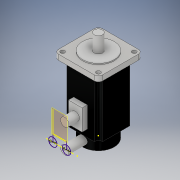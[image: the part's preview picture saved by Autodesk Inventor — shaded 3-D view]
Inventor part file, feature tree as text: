
AUTODESK INVENTOR PART (.ipt)
format: ipt  version: 2019.4 (Build 234330000, 330)  size: 254,464 bytes
history: native  units: mm
features: sketch x12, extrude x9, fillet x1, plane x1
ambient origin geometry x8: Origin, YZ Plane, XZ Plane, XY Plane, X Axis, Y Axis, Z Axis, Center Point
bodies: Solid1 (feature_tree)
feature tree (23):
  extrude  "Extrusion1"  Depth=34.0mm
  sketch  "Sketch4"  dims[d2=54.0mm d3=0.0mm d15=4.0mm]
  extrude  "Extrusion2"  Depth=4.0mm
  extrude  "Extrusion3"  Depth=4.0mm
  extrude  "Extrusion4"  Depth=5.0mm TaperAngle=0.0deg
  extrude  "Extrusion5"  TaperAngle=0.0deg  [1 undecoded]
  extrude  "Extrusion6"  Depth=17.0mm
  fillet  "Fillet1"  Radius=40.0mm
  extrude  "Extrusion7"  Depth=21.0mm
  plane  "Work Plane1"
  sketch  "Sketch12"  dims[d44=8.0mm d45=3.75mm]
  extrude  "Extrusion8"  Depth=1.0mm TaperAngle=0.0deg
  sketch  "Sketch14"  dims[d48=4.0mm]
  extrude  "Extrusion9"  Depth=3.75mm
  sketch  "Sketch1"  dims[d0=34.0mm d1=34.0mm]
  sketch  "Sketch5"  dims[d16=5.0mm d17=0.0mm d18=4.0mm]
  sketch  "Sketch6"  dims[d19=20.0mm d21=34.0mm d22=20.0mm d24=34.0mm d27=5.0mm d28=0.0mm]
  sketch  "Sketch8"  dims[d29=4.0mm d31=0.0mm]
  sketch  "Sketch9"  dims[d32=3.0mm d33=17.0mm d34=40.0mm d36=360.0deg]
  sketch  "Sketch10"  dims[d38=5.0mm d39=0.0mm d40=21.0mm]
  sketch  "Sketch11"  dims[d41=30.0mm d42=1.0mm d43=0.0mm]
  sketch  "Sketch13"  dims[d46=15.0mm d47=0.0mm]
  sketch  "Sketch15"  dims[d49=17.0mm d50=13.0mm d51=20.0mm d52=5.0mm d53=0.0mm d54=15.0mm d57=17.0mm d58=30.0mm d59=12.0mm d60=0.0mm d61=8.0mm d62=8.0mm d63=6.5mm d64=8.0mm d65=23.0mm d66=8.0mm d67=20.0mm d68=0.0mm]
note: 1 required parameter value undecoded (feature->parameter linkage not recoverable at this tier; creation-order binding heuristic only, values carry confidence <= 0.55)
